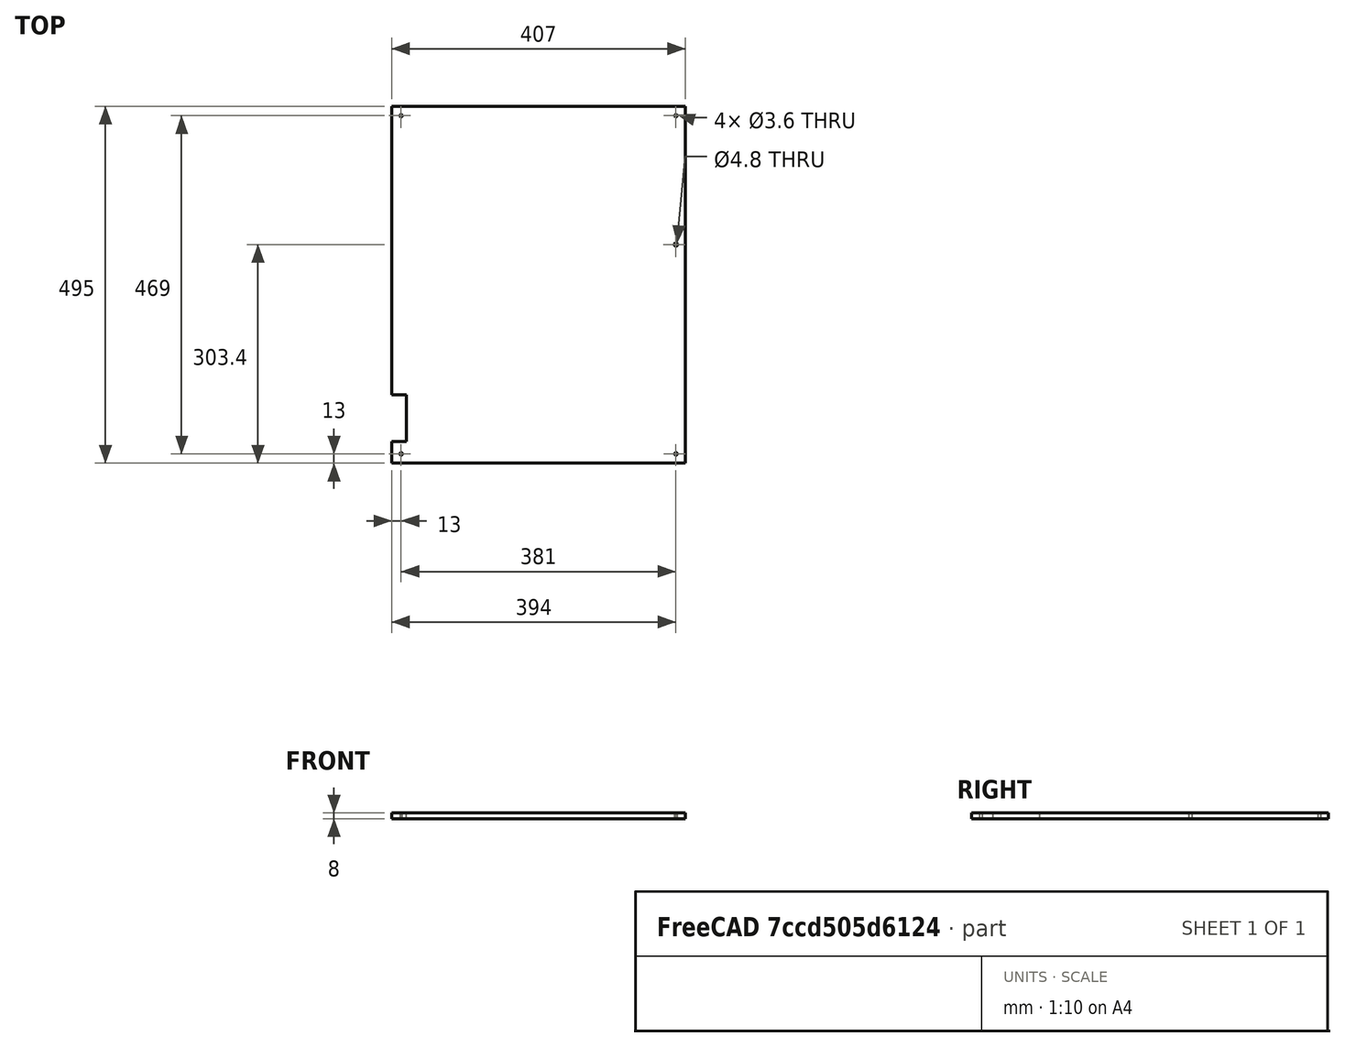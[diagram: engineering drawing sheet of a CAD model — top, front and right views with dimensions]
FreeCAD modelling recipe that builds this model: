
FCSTD DOCUMENT  (FreeCAD 0.16R6706 (Git))
Label: Lado Esquerdo
License: All rights reserved
LicenseURL: http://en.wikipedia.org/wiki/All_rights_reserved
objects: Sketcher::SketchObject×1, PartDesign::Pad×1
note: 3 computed .brp shape members not serialized (recipe doc carries the construction recipe); baked Part::Feature solids carry a one-line shape summary decoded from their .brp

FEATURE [Sketcher::SketchObject] Sketch
  sketch-geometry (17):
    g0: LineSegment StartX=-203.5 StartY=247.5 StartZ=0 EndX=203.5 EndY=247.5 EndZ=0
    g1: LineSegment StartX=203.5 StartY=247.5 StartZ=0 EndX=203.5 EndY=-247.5 EndZ=0
    g2: LineSegment StartX=203.5 StartY=-247.5 StartZ=0 EndX=-203.5 EndY=-247.5 EndZ=0
    g3: LineSegment StartX=-203.5 StartY=-247.5 StartZ=0 EndX=-203.5 EndY=-217.5 EndZ=0
    g4: LineSegment [constr] StartX=-190.5 StartY=234.5 StartZ=0 EndX=190.5 EndY=234.5 EndZ=0
    g5: LineSegment [constr] StartX=190.5 StartY=234.5 StartZ=0 EndX=190.5 EndY=-234.5 EndZ=0
    g6: LineSegment [constr] StartX=190.5 StartY=-234.5 StartZ=0 EndX=-190.5 EndY=-234.5 EndZ=0
    g7: LineSegment [constr] StartX=-190.5 StartY=-234.5 StartZ=0 EndX=-190.5 EndY=234.5 EndZ=0
    g8: Circle CenterX=-190.5 CenterY=234.5 CenterZ=0 NormalX=0 NormalY=0 NormalZ=1 Radius=1.8
    g9: Circle CenterX=190.5 CenterY=234.5 CenterZ=0 NormalX=0 NormalY=0 NormalZ=1 Radius=1.8
    g10: Circle CenterX=-190.5 CenterY=-234.5 CenterZ=0 NormalX=0 NormalY=0 NormalZ=1 Radius=1.8
    g11: Circle CenterX=190.5 CenterY=-234.5 CenterZ=0 NormalX=0 NormalY=0 NormalZ=1 Radius=1.8
    g12: Circle CenterX=190.5 CenterY=55.9 CenterZ=0 NormalX=0 NormalY=0 NormalZ=1 Radius=2.4
    g13: LineSegment StartX=-203.5 StartY=-152.5 StartZ=0 EndX=-183.5 EndY=-152.5 EndZ=0
    g14: LineSegment StartX=-183.5 StartY=-152.5 StartZ=0 EndX=-183.5 EndY=-217.5 EndZ=0
    g15: LineSegment StartX=-183.5 StartY=-217.5 StartZ=0 EndX=-203.5 EndY=-217.5 EndZ=0
    g16: LineSegment StartX=-203.5 StartY=-152.5 StartZ=0 EndX=-203.5 EndY=247.5 EndZ=0
  constraints (44):
    c: Coincident(g0,g1)
    c: Coincident(g1,g2)
    c: Coincident(g2,g3)
    c: Coincident(g16,g0)
    c: Horizontal(g0)
    c: Horizontal(g2)
    c: Vertical(g1)
    c: Vertical(g3)
    c: Symmetric(g2,g0,g-1)
    c: Coincident(g4,g5)
    c: Coincident(g5,g6)
    c: Coincident(g6,g7)
    c: Coincident(g7,g4)
    c: Horizontal(g4)
    c: Horizontal(g6)
    c: Vertical(g5)
    c: Vertical(g7)
    c: Symmetric(g4,g6,g-1)
    c: DistanceX(g0,g4) = 13
    c: DistanceY(g4,g0) = 13
    c: DistanceX(g0,g0) = 407
    c: DistanceY(g1,g1) = 495
    c: Radius(g8) = 1.8
    c: Equal(g8,g9) = 1.8
    c: Equal(g8,g10) = 1.8
    c: Equal(g8,g11) = 1.8
    c: Coincident(g4,g8)
    c: Coincident(g10,g6)
    c: Coincident(g11,g5)
    c: Coincident(g4,g9)
    c: Radius(g12) = 2.4
    c: DistanceY(g12,g0) = 191.6
    c: Coincident(g13,g14)
    c: Coincident(g14,g15)
    c: Horizontal(g13)
    c: Horizontal(g15)
    c: Vertical(g14)
    c: DistanceY(g2,g14) = 30
    c: DistanceY(g14,g14) = 65
    c: Tangent(g3,g16)
    c: Coincident(g13,g16)
    c: Coincident(g15,g3)
    c: DistanceX(g15,g15) = 20
    c: PointOnObject(g12,g5)
FEATURE [PartDesign::Pad] Pad
  Length = 8
  Length2 = 100
  Sketch = -> Sketch
  Type = 0
